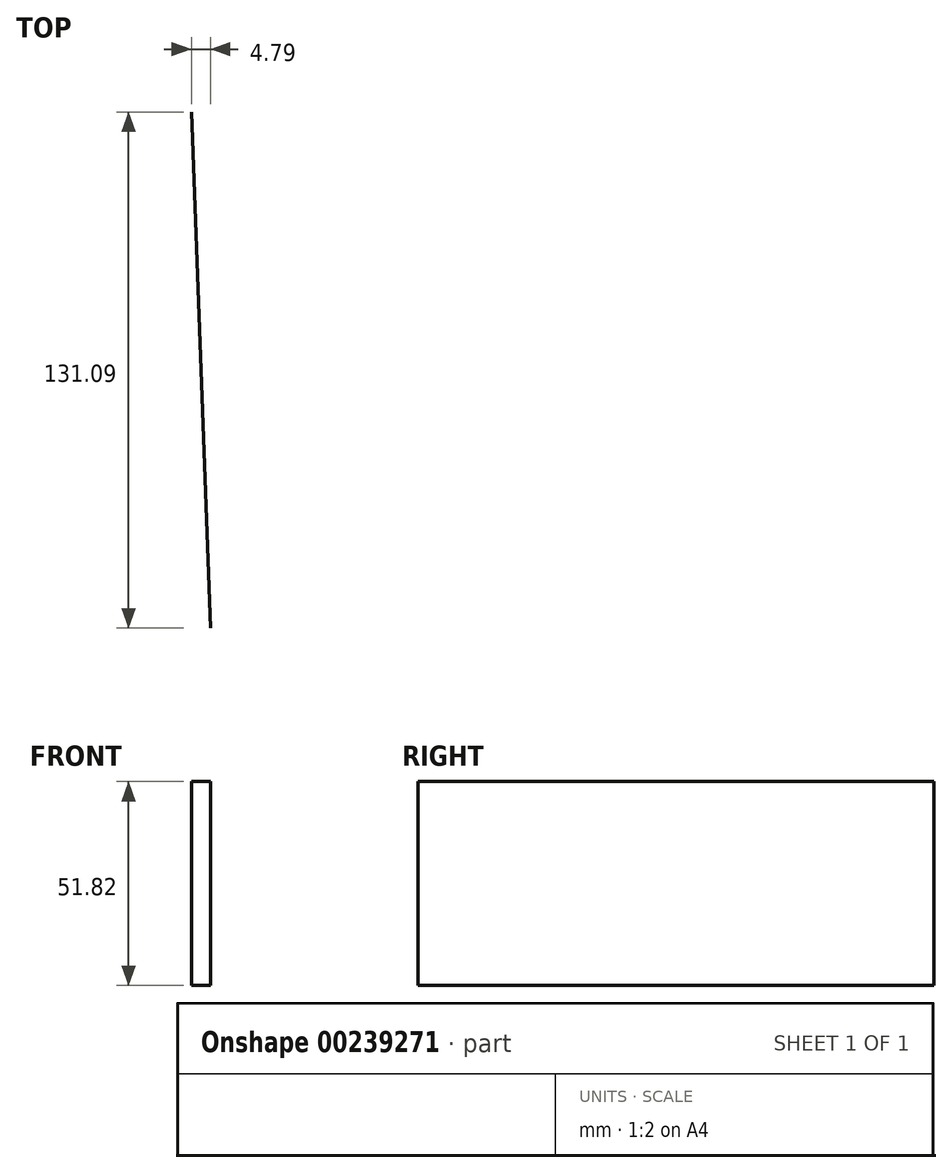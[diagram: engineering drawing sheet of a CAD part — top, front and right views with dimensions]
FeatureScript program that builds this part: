
annotation { "Feature Type Name" : "Feature", "Feature Type Description" : "" }
export const myFeature = defineFeature(function(context is Context, id is Id, definition is map)
    precondition{}
    {
        {
            var Q0;
            Q0=qCreatedBy(makeId("Top.planeOp"),FACE);
            var sketch = newSketch(context, id + "F0", { "sketchPlane" : qUnion([Q0])});
            skLineSegment(sketch, "E0", {"start": v(-126.58, -60.11) * mm, "end": v(-131.37, 70.98) * mm});
            skLineSegment(sketch, "E1", {"start": v(-131.37, 70.98) * mm, "end": v(116.21, 70.98) * mm});
            skLineSegment(sketch, "E2", {"start": v(116.21, 70.98) * mm, "end": v(116.21, -60.11) * mm});
            skLineSegment(sketch, "E3", {"start": v(116.21, -60.11) * mm, "end": v(-126.58, -60.11) * mm});
            skSolve(sketch);
        }
        {
            var Q0;
            Q0=sQuery(id+"F0.wireOp",EDGE,"E0");
            extrude(context, id + "F1", {"bodyType" : ToolBodyType.SURFACE, "surfaceEntities" : qUnion([Q0]), "depth" : 51.82 * mm});
        }
    });
